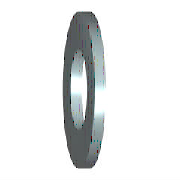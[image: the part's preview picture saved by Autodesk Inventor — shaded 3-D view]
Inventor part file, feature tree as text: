
AUTODESK INVENTOR PART (.ipt)
format: ipt  version: 2018 (Build 220112000, 112)  size: 104,448 bytes
history: native  units: mm (DEFAULTED — no unit token found)
features: other x1, plane x1, sketch x1
ambient origin geometry x7: Origin, YZ Plane, XY Plane, X Axis, Y Axis, Z Axis, Center Point
bodies: Solid1 (feature_tree), Body (feature_tree)
feature tree (3):
  other  "Work Axis1"
  plane  "Work Plane1"
  sketch  "Sketch"  dims[d0=5.3mm d1=15.0mm d2=1.2mm d3=0.0mm d4=0.0mm d5=0.0mm d6=0.0mm d7=0.0mm]
